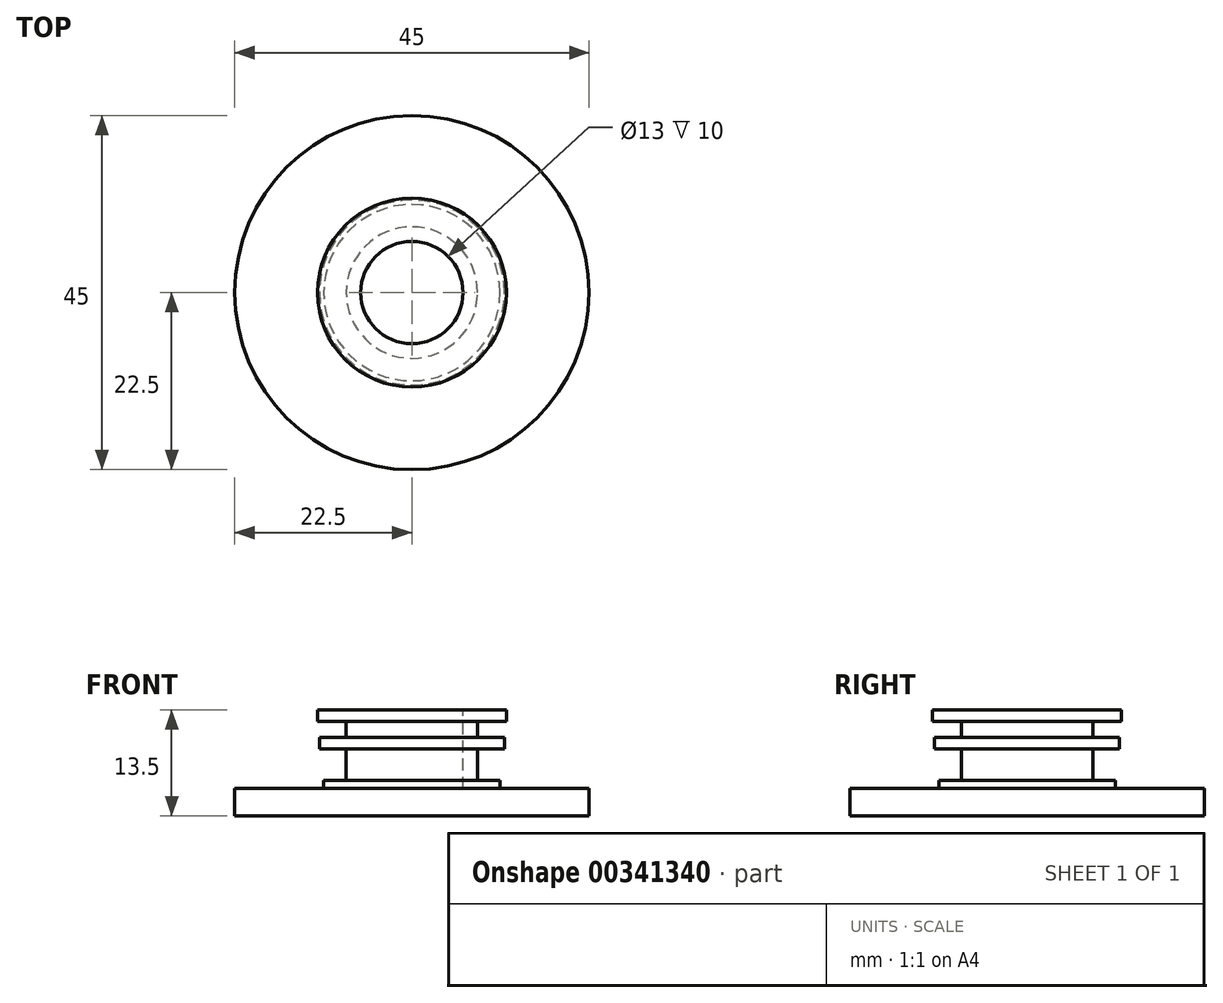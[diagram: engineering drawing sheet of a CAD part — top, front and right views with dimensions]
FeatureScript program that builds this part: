
annotation { "Feature Type Name" : "Feature", "Feature Type Description" : "" }
export const myFeature = defineFeature(function(context is Context, id is Id, definition is map)
    precondition{}
    {
        {
            var Q0;
            Q0=qCreatedBy(makeId("Top.planeOp"),FACE);
            var sketch = newSketch(context, id + "F0", { "sketchPlane" : qUnion([Q0])});
            skCircle(sketch, "E0", {"center": v(0, 0) * mm, "radius": 22.5 * mm});
            skSolve(sketch);
        }
        {
            var Q0;
            Q0 = qSketchRegion(id + "F0", true);
            extrude(context, id + "F1", {"entities" : qUnion([Q0]), "depth" : 3.5 * mm});
        }
        {
            var Q0;
            Q0=makeQuery(id+"F1.opExtrude","CAP_FACE",FACE,{"disambiguationData":[OSD([sQuery(id+"F0.wireOp",EDGE,"E0")])],"isStart":false});
            var sketch = newSketch(context, id + "F2", { "sketchPlane" : qUnion([Q0])});
            skCircle(sketch, "E1", {"center": v(0, 0) * mm, "radius": 11.2 * mm});
            skSolve(sketch);
        }
        {
            var Q0;
            Q0 = qSketchRegion(id + "F2", true);
            extrude(context, id + "F3", {"entities" : qUnion([Q0]), "operationType" : NewBodyOperationType.ADD, "depth" : 1 * mm});
        }
        {
            var Q0;
            Q0=makeQuery(id+"F3.opExtrude","CAP_FACE",FACE,{"disambiguationData":[OSD([sQuery(id+"F2.wireOp",EDGE,"E1")])],"isStart":false});
            var sketch = newSketch(context, id + "F4", { "sketchPlane" : qUnion([Q0])});
            skCircle(sketch, "E2", {"center": v(0, 0) * mm, "radius": 8.35 * mm});
            skSolve(sketch);
        }
        {
            var Q0;
            Q0 = qSketchRegion(id + "F4", true);
            extrude(context, id + "F5", {"entities" : qUnion([Q0]), "operationType" : NewBodyOperationType.ADD, "depth" : 4 * mm});
        }
        {
            var Q0;
            Q0=makeQuery(id+"F5.opExtrude","CAP_FACE",FACE,{"disambiguationData":[OSD([sQuery(id+"F4.wireOp",EDGE,"E2")])],"isStart":false});
            var sketch = newSketch(context, id + "F6", { "sketchPlane" : qUnion([Q0])});
            skCircle(sketch, "E3", {"center": v(0, 0) * mm, "radius": 11.75 * mm});
            skSolve(sketch);
        }
        {
            var Q0;
            Q0 = qSketchRegion(id + "F6", true);
            extrude(context, id + "F7", {"entities" : qUnion([Q0]), "operationType" : NewBodyOperationType.ADD, "depth" : 1.5 * mm});
        }
        {
            var Q0;
            Q0=makeQuery(id+"F7.opExtrude","CAP_FACE",FACE,{"disambiguationData":[OSD([sQuery(id+"F6.wireOp",EDGE,"E3")])],"isStart":false});
            var sketch = newSketch(context, id + "F8", { "sketchPlane" : qUnion([Q0])});
            skCircle(sketch, "E4", {"center": v(0, 0) * mm, "radius": 8.35 * mm});
            skSolve(sketch);
        }
        {
            var Q0;
            Q0 = qSketchRegion(id + "F8", true);
            extrude(context, id + "F9", {"entities" : qUnion([Q0]), "operationType" : NewBodyOperationType.ADD, "depth" : 2 * mm});
        }
        {
            var Q0;
            Q0=makeQuery(id+"F9.opExtrude","CAP_FACE",FACE,{"disambiguationData":[OSD([sQuery(id+"F8.wireOp",EDGE,"E4")])],"isStart":false});
            var sketch = newSketch(context, id + "F10", { "sketchPlane" : qUnion([Q0])});
            skCircle(sketch, "E5", {"center": v(0, 0) * mm, "radius": 12 * mm});
            skSolve(sketch);
        }
        {
            var Q0;
            Q0 = qSketchRegion(id + "F10", true);
            extrude(context, id + "F11", {"entities" : qUnion([Q0]), "operationType" : NewBodyOperationType.ADD, "depth" : 1.5 * mm});
        }
        {
            var Q0;
            Q0=makeQuery(id+"F11.opExtrude","CAP_FACE",FACE,{"disambiguationData":[OSD([sQuery(id+"F10.wireOp",EDGE,"E5")])],"isStart":false});
            var sketch = newSketch(context, id + "F12", { "sketchPlane" : qUnion([Q0])});
            skCircle(sketch, "E6", {"center": v(0, 0) * mm, "radius": 6.5 * mm});
            skSolve(sketch);
        }
        {
            var Q0;
            Q0=makeQuery(id+"F12.imprint","IMPRINT",FACE,{"disambiguationData":[TD([[makeQuery(id+"F12.imprint","IMPRINT",EDGE,{"derivedFrom":sQuery(id+"F12.wireOp",EDGE,"E6")}),1.0]])]});
            var Q1;
            Q1=makeQuery(id+"F1.opExtrude","CAP_FACE",FACE,{"disambiguationData":[OSD([sQuery(id+"F0.wireOp",EDGE,"E0")])],"isStart":false});
            extrude(context, id + "F13", {"entities" : qUnion([Q0]), "operationType" : NewBodyOperationType.REMOVE, "endBound" : BoundingType.UP_TO_SURFACE, "oppositeDirection" : true, "endBoundEntityFace" : qUnion([Q1]), "depth" : 20.7 * mm});
        }
    });
